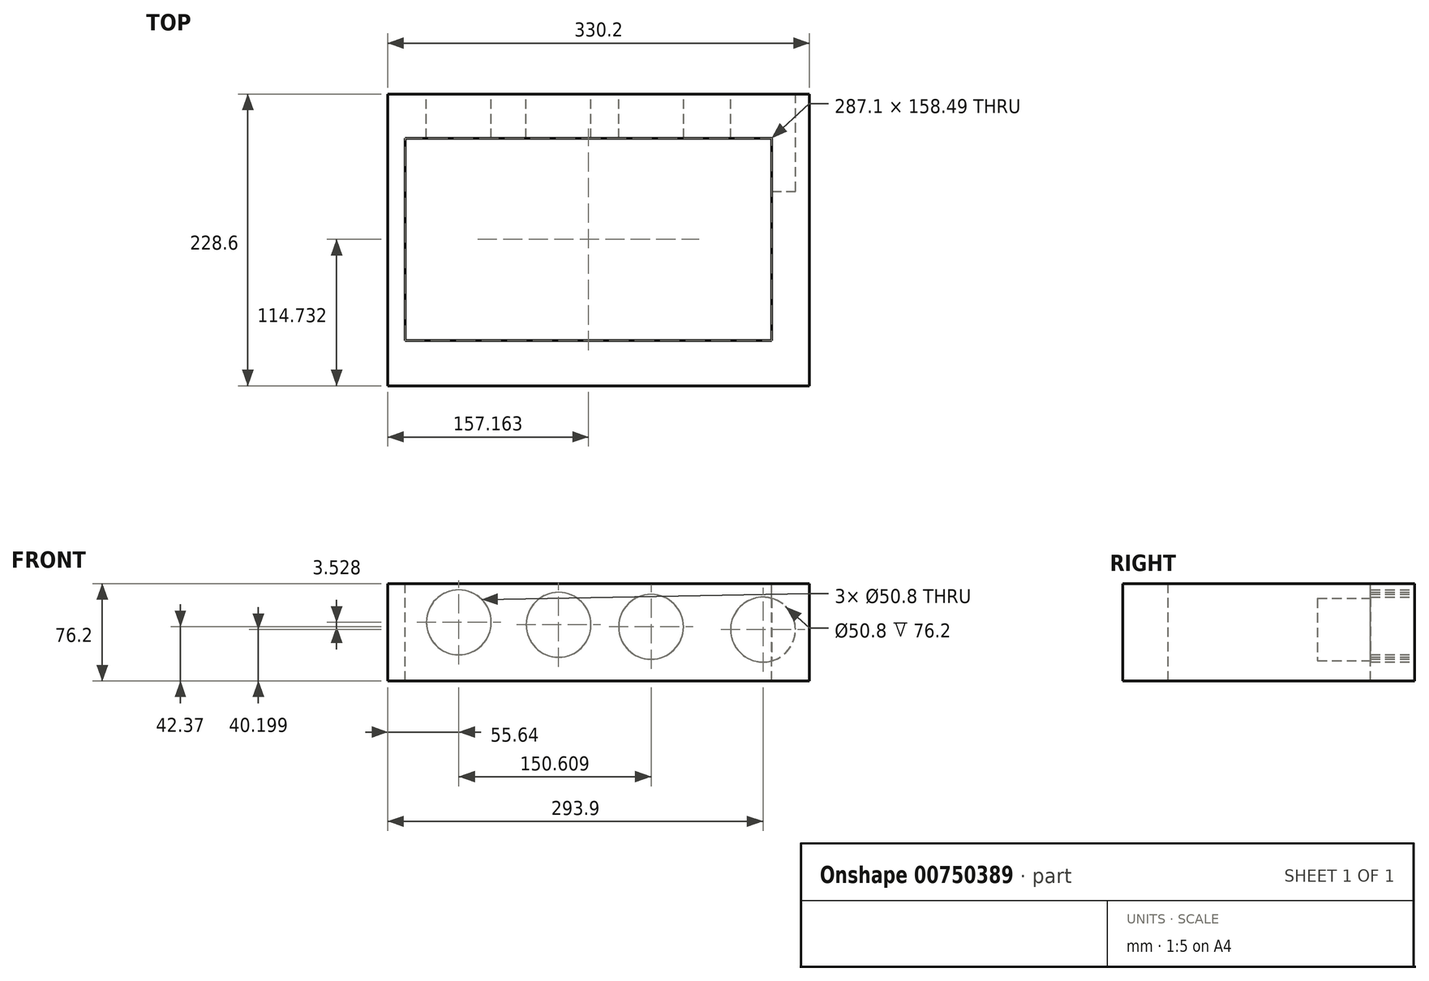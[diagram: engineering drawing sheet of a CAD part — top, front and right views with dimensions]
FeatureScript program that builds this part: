
annotation { "Feature Type Name" : "Feature", "Feature Type Description" : "" }
export const myFeature = defineFeature(function(context is Context, id is Id, definition is map)
    precondition{}
    {
        {
            var Q0;
            Q0=qCreatedBy(makeId("Top.planeOp"),FACE);
            var sketch = newSketch(context, id + "F0", { "sketchPlane" : qUnion([Q0])});
            skLineSegment(sketch, "E0.bottom", {"start": v(-147.3, -76.42) * mm, "end": v(182.9, -76.42) * mm});
            skLineSegment(sketch, "E0.top", {"start": v(-147.3, 152.18) * mm, "end": v(182.9, 152.18) * mm});
            skLineSegment(sketch, "E0.left", {"start": v(-147.3, -76.42) * mm, "end": v(-147.3, 152.18) * mm});
            skLineSegment(sketch, "E0.right", {"start": v(182.9, -76.42) * mm, "end": v(182.9, 152.18) * mm});
            skSolve(sketch);
        }
        {
            var Q0;
            Q0=makeQuery(id+"F0.imprint","IMPRINT",FACE,{"disambiguationData":[TD([[makeQuery(id+"F0.imprint","IMPRINT",EDGE,{"derivedFrom":sQuery(id+"F0.wireOp",EDGE,"E0.bottom")}),1.0]])]});
            extrude(context, id + "F1", {"entities" : qUnion([Q0]), "depth" : 76.2 * mm, "offsetDistance" : 25.4 * mm});
        }
        {
            var Q0;
            Q0=makeQuery(id+"F1.opExtrude","SWEPT_FACE",FACE,{"disambiguationData":[OSD([sQuery(id+"F0.wireOp",EDGE,"E0.top")])]});
            var sketch = newSketch(context, id + "F2", { "sketchPlane" : qUnion([Q0])});
            skCircle(sketch, "E1", {"center": v(-146.6, 40.2) * mm, "radius": 25.4 * mm});
            skCircle(sketch, "E2", {"center": v(-58.96, 42.37) * mm, "radius": 25.4 * mm});
            skCircle(sketch, "E3", {"center": v(13.5, 44) * mm, "radius": 25.4 * mm});
            skCircle(sketch, "E4", {"center": v(91.65, 45.9) * mm, "radius": 25.4 * mm});
            skSolve(sketch);
        }
        {
            var Q0;
            Q0=makeQuery(id+"F1.opExtrude","CAP_FACE",FACE,{"disambiguationData":[OSD([sQuery(id+"F0.wireOp",EDGE,"E0.bottom"),sQuery(id+"F0.wireOp",EDGE,"E0.top"),sQuery(id+"F0.wireOp",EDGE,"E0.left"),sQuery(id+"F0.wireOp",EDGE,"E0.right")])],"isStart":false});
            var sketch = newSketch(context, id + "F3", { "sketchPlane" : qUnion([Q0])});
            skPoint(sketch, "E5", {"position": v(0, 37.88) * mm});
            skPoint(sketch, "E5.positionSnap0", {"position": v(182.9, 37.88) * mm});
            skSolve(sketch);
        }
        {
            var Q0;
            Q0=makeQuery(id+"F3.imprint","IMPRINT",FACE,{"disambiguationData":[TD([[makeQuery(id+"F3.imprint","IMPRINT",EDGE,{"derivedFrom":makeQuery(id+"F1.opExtrude","CAP_EDGE",EDGE,{"disambiguationData":[OSD([sQuery(id+"F0.wireOp",EDGE,"E0.bottom")])],"isStart":false})}),1.0]])]});
            var sketch = newSketch(context, id + "F4", { "sketchPlane" : qUnion([Q0])});
            skPoint(sketch, "E6", {"position": v(9.87, 38.31) * mm});
            skLineSegment(sketch, "E7.bottom", {"start": v(-133.68, 117.56) * mm, "end": v(153.43, 117.56) * mm});
            skLineSegment(sketch, "E7.top", {"start": v(-133.68, -40.93) * mm, "end": v(153.43, -40.93) * mm});
            skLineSegment(sketch, "E7.left", {"start": v(-133.68, 117.56) * mm, "end": v(-133.68, -40.93) * mm});
            skLineSegment(sketch, "E7.right", {"start": v(153.43, 117.56) * mm, "end": v(153.43, -40.93) * mm});
            skSolve(sketch);
        }
        {
            var Q0;
            Q0=makeQuery(id+"F4.imprint","IMPRINT",FACE,{"disambiguationData":[TD([[makeQuery(id+"F4.imprint","IMPRINT",EDGE,{"derivedFrom":sQuery(id+"F4.wireOp",EDGE,"E7.bottom")}),-1.0]])]});
            extrude(context, id + "F5", {"entities" : qUnion([Q0]), "operationType" : NewBodyOperationType.REMOVE, "oppositeDirection" : true, "depth" : 127 * mm, "offsetDistance" : 25.4 * mm});
        }
        {
            var Q0;
            Q0=makeQuery(id+"F2.imprint","IMPRINT",FACE,{"disambiguationData":[TD([[makeQuery(id+"F2.imprint","IMPRINT",EDGE,{"derivedFrom":sQuery(id+"F2.wireOp",EDGE,"E1")}),1.0]])]});
            var Q1;
            Q1=makeQuery(id+"F2.imprint","IMPRINT",FACE,{"disambiguationData":[TD([[makeQuery(id+"F2.imprint","IMPRINT",EDGE,{"derivedFrom":sQuery(id+"F2.wireOp",EDGE,"E2")}),1.0]])]});
            var Q2;
            Q2=makeQuery(id+"F2.imprint","IMPRINT",FACE,{"disambiguationData":[TD([[makeQuery(id+"F2.imprint","IMPRINT",EDGE,{"derivedFrom":sQuery(id+"F2.wireOp",EDGE,"E3")}),1.0]])]});
            var Q3;
            Q3=makeQuery(id+"F2.imprint","IMPRINT",FACE,{"disambiguationData":[TD([[makeQuery(id+"F2.imprint","IMPRINT",EDGE,{"derivedFrom":sQuery(id+"F2.wireOp",EDGE,"E4")}),1.0]])]});
            extrude(context, id + "F6", {"entities" : qUnion([Q0, Q1, Q2, Q3]), "operationType" : NewBodyOperationType.ADD, "depth" : 76.2 * mm, "offsetDistance" : 25.4 * mm});
        }
        {
            var Q0;
            Q0=makeQuery(id+"F6.opExtrude","CAP_FACE",FACE,{"disambiguationData":[OSD([sQuery(id+"F2.wireOp",EDGE,"E1")])],"isStart":false});
            var Q1;
            Q1=makeQuery(id+"F6.opExtrude","CAP_FACE",FACE,{"disambiguationData":[OSD([sQuery(id+"F2.wireOp",EDGE,"E2")])],"isStart":false});
            var Q2;
            Q2=makeQuery(id+"F6.opExtrude","CAP_FACE",FACE,{"disambiguationData":[OSD([sQuery(id+"F2.wireOp",EDGE,"E3")])],"isStart":false});
            var Q3;
            Q3=makeQuery(id+"F6.opExtrude","CAP_FACE",FACE,{"disambiguationData":[OSD([sQuery(id+"F2.wireOp",EDGE,"E4")])],"isStart":false});
            extrude(context, id + "F7", {"entities" : qUnion([Q0, Q1, Q2, Q3]), "operationType" : NewBodyOperationType.REMOVE, "oppositeDirection" : true, "depth" : 152.4 * mm, "offsetDistance" : 25.4 * mm});
        }
    });
